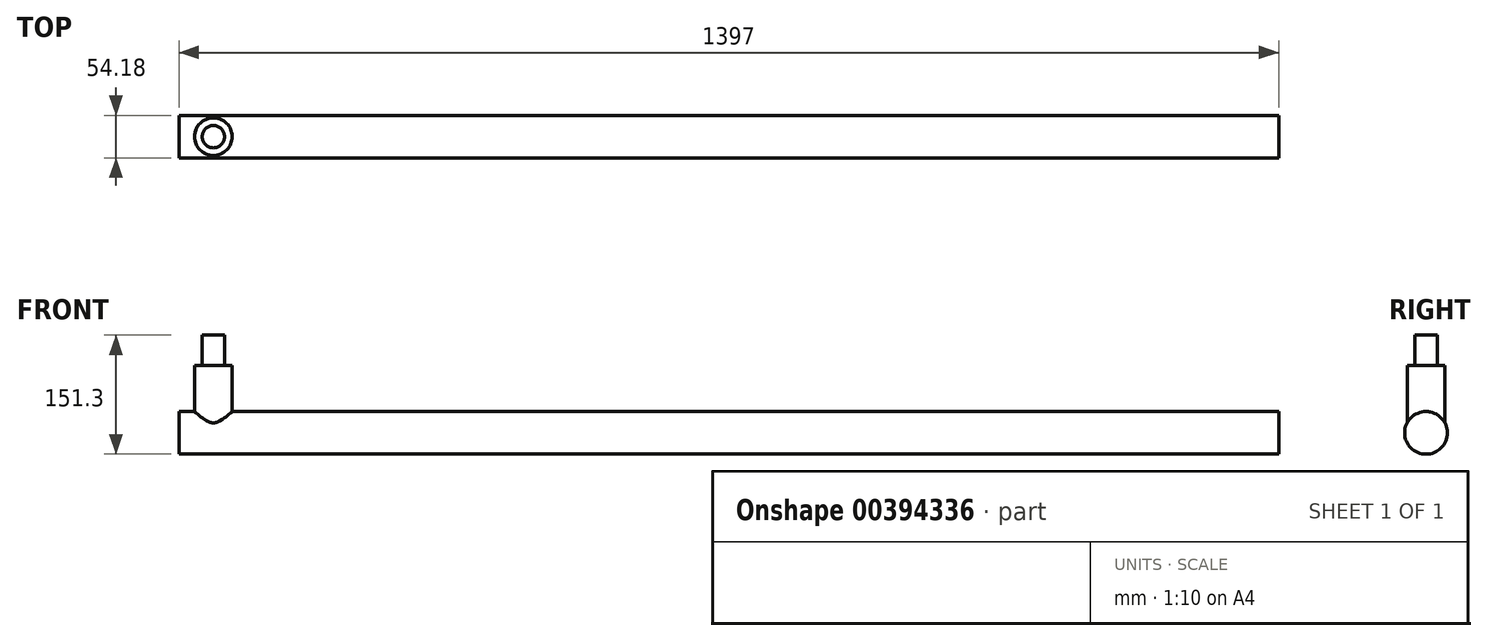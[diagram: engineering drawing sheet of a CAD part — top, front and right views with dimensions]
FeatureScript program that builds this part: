
annotation { "Feature Type Name" : "Feature", "Feature Type Description" : "" }
export const myFeature = defineFeature(function(context is Context, id is Id, definition is map)
    precondition{}
    {
        {
            var Q0;
            Q0=qCreatedBy(makeId("Right.planeOp"),FACE);
            var sketch = newSketch(context, id + "F0", { "sketchPlane" : qUnion([Q0])});
            skCircle(sketch, "E0", {"center": v(0, 0) * mm, "radius": 27.09 * mm});
            skSolve(sketch);
        }
        {
            var Q0;
            Q0 = qSketchRegion(id + "F0", true);
            extrude(context, id + "F1", {"entities" : qUnion([Q0]), "depth" : 1397 * mm});
        }
        {
            var Q0;
            Q0=qCreatedBy(makeId("Top.planeOp"),FACE);
            var sketch = newSketch(context, id + "F2", { "sketchPlane" : qUnion([Q0])});
            skCircle(sketch, "E1", {"center": v(43.75, 0) * mm, "radius": 23.9 * mm});
            skSolve(sketch);
        }
        {
            var Q0;
            Q0 = qSketchRegion(id + "F2", true);
            extrude(context, id + "F3", {"entities" : qUnion([Q0]), "operationType" : NewBodyOperationType.ADD, "depth" : 85.85 * mm});
        }
        {
            var Q0;
            Q0=makeQuery(id+"F3.opExtrude","CAP_FACE",FACE,{"disambiguationData":[OSD([sQuery(id+"F2.wireOp",EDGE,"E1")])],"isStart":false});
            var sketch = newSketch(context, id + "F4", { "sketchPlane" : qUnion([Q0])});
            skCircle(sketch, "E2", {"center": v(43.75, 0) * mm, "radius": 14.2 * mm});
            skSolve(sketch);
        }
        {
            var Q0;
            Q0 = qSketchRegion(id + "F4", true);
            extrude(context, id + "F5", {"entities" : qUnion([Q0]), "operationType" : NewBodyOperationType.ADD, "depth" : 38.35 * mm});
        }
    });
